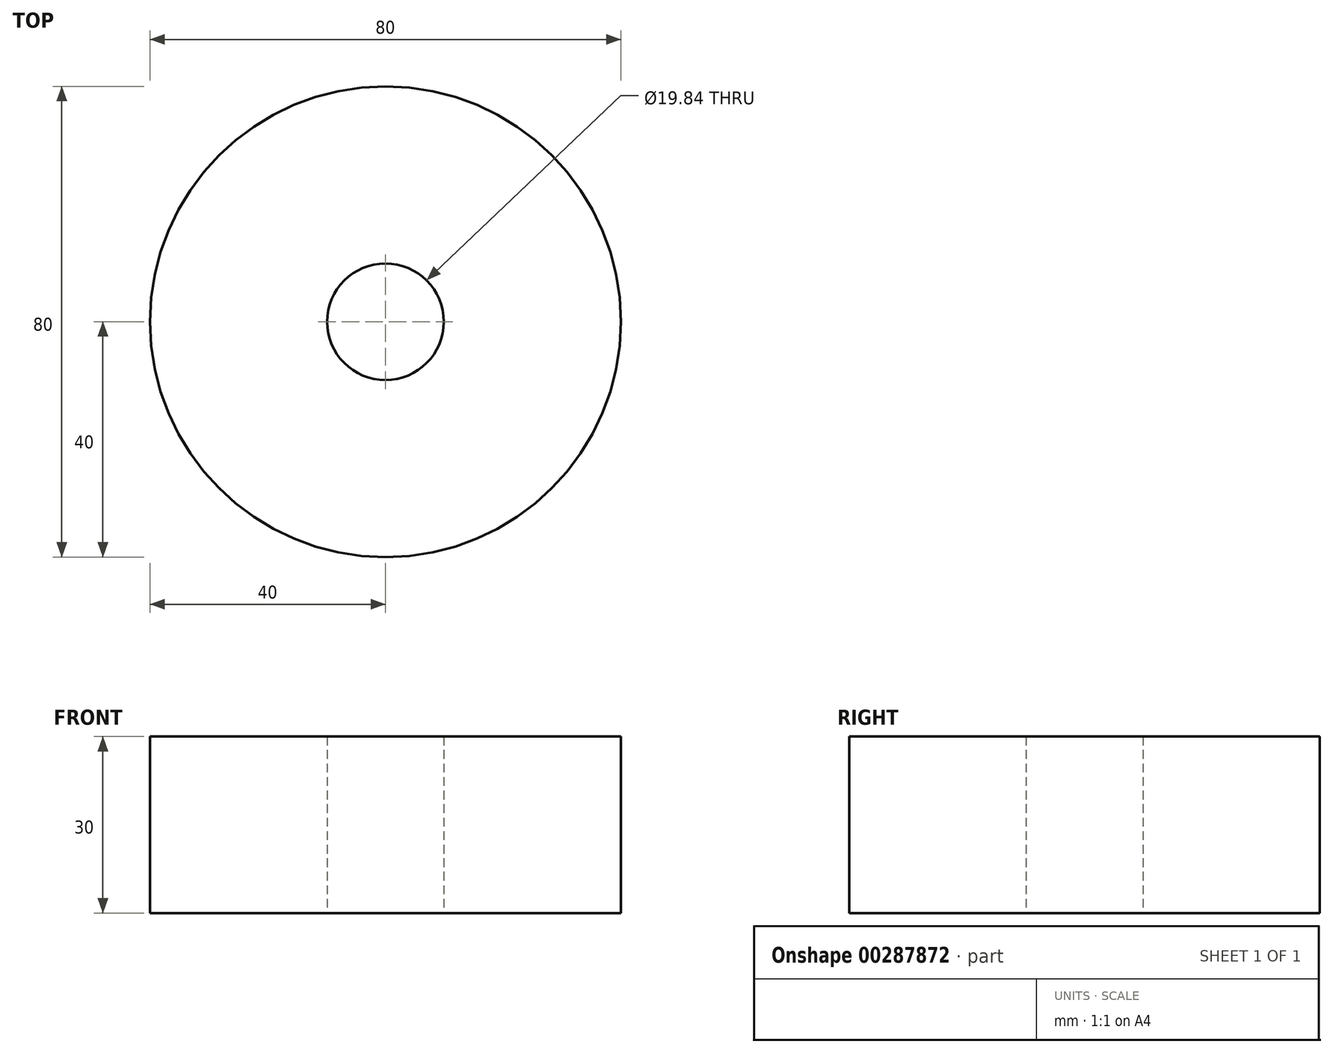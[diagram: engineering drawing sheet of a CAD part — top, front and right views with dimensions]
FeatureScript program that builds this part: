
annotation { "Feature Type Name" : "Feature", "Feature Type Description" : "" }
export const myFeature = defineFeature(function(context is Context, id is Id, definition is map)
    precondition{}
    {
        {
            var Q0;
            Q0=qCreatedBy(makeId("Top.planeOp"),FACE);
            var sketch = newSketch(context, id + "F0", { "sketchPlane" : qUnion([Q0])});
            skCircle(sketch, "E0", {"center": v(0, 0) * mm, "radius": 40 * mm});
            skCircle(sketch, "E1", {"center": v(0, 0) * mm, "radius": 9.92 * mm});
            skSolve(sketch);
        }
        {
            var Q0;
            Q0 = qSketchRegion(id + "F0", true);
            extrude(context, id + "F1", {"entities" : qUnion([Q0]), "depth" : 30 * mm});
        }
    });
